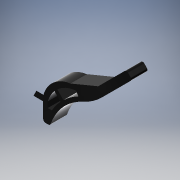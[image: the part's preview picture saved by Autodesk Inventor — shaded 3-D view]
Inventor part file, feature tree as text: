
AUTODESK INVENTOR PART (.ipt)
format: ipt  version: 2018 (Build 220112000, 112)  size: 219,136 bytes
history: native  units: mm
features: extrude x7, sketch x6, fillet x3, chamfer x1
ambient origin geometry x8: Origin, YZ Plane, XZ Plane, XY Plane, X Axis, Y Axis, Z Axis, Center Point
bodies: Body1 (feature_tree)
feature tree (17):
  extrude  "Extrusión5"  Depth=20.0mm
  fillet  "Empalme3"  Radius=70.0mm
  fillet  "Empalme4"  [1 undecoded]
  fillet  "Empalme5"  Radius=10.0mm
  chamfer  "Chaflán1"  Distance=20.0mm
  extrude  "Extrusión6"  Depth=3.0mm
  extrude  "Extrusión7"  Depth=20.0mm TaperAngle=45.0deg
  extrude  "Extrusión8"  TaperAngle=150.0deg  [1 undecoded]
  extrude  "Extrusión9"  Depth=5.0mm
  extrude  "Extrusión10"  Depth=40.0mm
  extrude  "Extrusión11"  Depth=20.0mm TaperAngle=0.0deg
  sketch  "Boceto1"  dims[d4=5.0mm d5=25.0mm d21=70.0mm d22=135.0deg d23=10.0mm d27=20.0mm d28=0.0mm]
  sketch  "Boceto4"  dims[d29=80.0mm d30=3.0mm]
  sketch  "Boceto5"  dims[d31=30.0mm d32=20.0mm d33=2.0mm d34=45.0deg]
  sketch  "Boceto6"  dims[d35=80.0mm d36=150.0deg]
  sketch  "Boceto7"  dims[d37=6.981317mm d38=5.0mm]
  sketch  "Boceto9"  dims[d39=7.0mm d40=40.0mm d41=20.0mm d42=0.0mm d43=40.0mm d44=30.0mm d48=20.0mm d49=0.0mm d50=44.831888mm d51=20.0mm d52=0.0mm d54=20.0mm d55=0.0mm d59=10.0mm d61=10.0mm d62=2.5mm d63=2.5mm d64=13.0mm d65=0.0mm d67=5.0mm d68=7.0mm d69=10.0mm d70=5.0mm d71=0.0mm]
note: 2 required parameter values undecoded (feature->parameter linkage not recoverable at this tier; creation-order binding heuristic only, values carry confidence <= 0.55)
